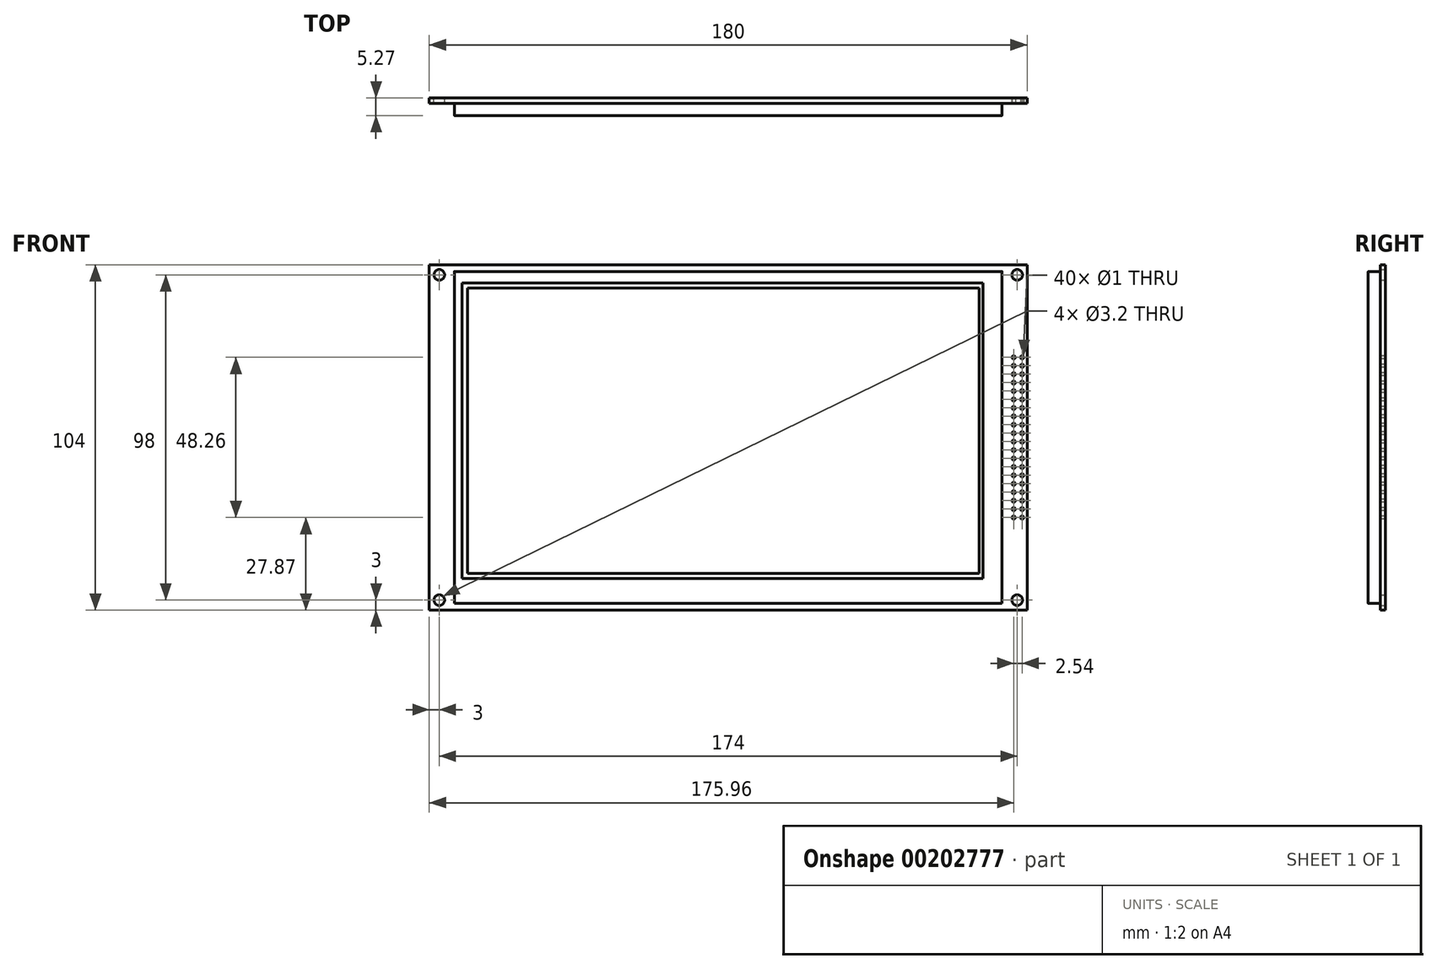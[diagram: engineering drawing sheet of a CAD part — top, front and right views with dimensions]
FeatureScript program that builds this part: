
annotation { "Feature Type Name" : "Feature", "Feature Type Description" : "" }
export const myFeature = defineFeature(function(context is Context, id is Id, definition is map)
    precondition{}
    {
        {
            var Q0;
            Q0=qCreatedBy(makeId("Front.planeOp"),FACE);
            var sketch = newSketch(context, id + "F0", { "sketchPlane" : qUnion([Q0])});
            skLineSegment(sketch, "E0.bottom", {"start": v(90, -52) * mm, "end": v(-90, -52) * mm});
            skLineSegment(sketch, "E0.top", {"start": v(90, 52) * mm, "end": v(-90, 52) * mm});
            skLineSegment(sketch, "E0.left", {"start": v(90, -52) * mm, "end": v(90, 52) * mm});
            skLineSegment(sketch, "E0.right", {"start": v(-90, -52) * mm, "end": v(-90, 52) * mm});
            skPoint(sketch, "E0.middle", {"position": v(0, 0) * mm});
            skCircle(sketch, "E1", {"center": v(-87, -49) * mm, "radius": 1.6 * mm});
            skCircle(sketch, "E2.0.1.0", {"center": v(-87, 49) * mm, "radius": 1.6 * mm});
            skCircle(sketch, "E2.1.0.0", {"center": v(87, -49) * mm, "radius": 1.6 * mm});
            skCircle(sketch, "E2.1.1.0", {"center": v(87, 49) * mm, "radius": 1.6 * mm});
            skLineSegment(sketch, "E2.direction1", {"start": v(-87, -49) * mm, "end": v(87, -49) * mm, "construction": true});
            skLineSegment(sketch, "E2.direction2", {"start": v(-87, -49) * mm, "end": v(-87, 49) * mm, "construction": true});
            skSolve(sketch);
        }
        {
            var Q0;
            Q0=makeQuery(id+"F0.imprint","IMPRINT",FACE,{"disambiguationData":[TD([[makeQuery(id+"F0.imprint","IMPRINT",EDGE,{"derivedFrom":sQuery(id+"F0.wireOp",EDGE,"E0.bottom")}),-1.0]])]});
            extrude(context, id + "F1", {"entities" : qUnion([Q0]), "depth" : 1.57 * mm});
        }
        {
            var Q0;
            Q0=makeQuery(id+"F1.opExtrude","CAP_FACE",FACE,{"disambiguationData":[OSD([sQuery(id+"F0.wireOp",EDGE,"E0.bottom"),sQuery(id+"F0.wireOp",EDGE,"E0.top"),sQuery(id+"F0.wireOp",EDGE,"E0.left"),sQuery(id+"F0.wireOp",EDGE,"E0.right"),sQuery(id+"F0.wireOp",EDGE,"E1"),sQuery(id+"F0.wireOp",EDGE,"E2.0.1.0"),sQuery(id+"F0.wireOp",EDGE,"E2.1.0.0"),sQuery(id+"F0.wireOp",EDGE,"E2.1.1.0")])],"isStart":false});
            var sketch = newSketch(context, id + "F2", { "sketchPlane" : qUnion([Q0])});
            skLineSegment(sketch, "E3", {"start": v(-82.45, -50) * mm, "end": v(82.45, -50) * mm});
            skLineSegment(sketch, "E4", {"start": v(-82.45, -50) * mm, "end": v(-82.45, 50) * mm});
            skLineSegment(sketch, "E5", {"start": v(-82.45, 50) * mm, "end": v(82.45, 50) * mm});
            skLineSegment(sketch, "E6", {"start": v(82.45, 50) * mm, "end": v(82.45, -50) * mm});
            skSolve(sketch);
        }
        {
            var Q0;
            Q0=makeQuery(id+"F2.imprint","IMPRINT",FACE,{"disambiguationData":[TD([[makeQuery(id+"F2.imprint","IMPRINT",EDGE,{"derivedFrom":sQuery(id+"F2.wireOp",EDGE,"E3")}),1.0]])]});
            extrude(context, id + "F3", {"entities" : qUnion([Q0]), "operationType" : NewBodyOperationType.ADD, "depth" : 3.7 * mm});
        }
        {
            var Q0;
            Q0=makeQuery(id+"F3.opExtrude","CAP_FACE",FACE,{"disambiguationData":[OSD([sQuery(id+"F2.wireOp",EDGE,"E3"),sQuery(id+"F2.wireOp",EDGE,"E4"),sQuery(id+"F2.wireOp",EDGE,"E5"),sQuery(id+"F2.wireOp",EDGE,"E6")])],"isStart":false});
            var sketch = newSketch(context, id + "F4", { "sketchPlane" : qUnion([Q0])});
            skLineSegment(sketch, "E7", {"start": v(-80.15, -42.5) * mm, "end": v(76.75, -42.5) * mm});
            skLineSegment(sketch, "E8", {"start": v(-80.15, -42.5) * mm, "end": v(-80.15, 46.5) * mm});
            skLineSegment(sketch, "E9", {"start": v(-80.15, 46.5) * mm, "end": v(76.75, 46.5) * mm});
            skLineSegment(sketch, "E10", {"start": v(76.75, 46.5) * mm, "end": v(76.75, -42.5) * mm});
            skSolve(sketch);
        }
        {
            var Q0;
            Q0=makeQuery(id+"F4.imprint","IMPRINT",FACE,{"disambiguationData":[TD([[makeQuery(id+"F4.imprint","IMPRINT",EDGE,{"derivedFrom":sQuery(id+"F4.wireOp",EDGE,"E7")}),1.0]])]});
            extrude(context, id + "F5", {"entities" : qUnion([Q0]), "operationType" : NewBodyOperationType.REMOVE, "oppositeDirection" : true, "depth" : .2 * mm});
        }
        {
            var Q0;
            Q0=makeQuery(id+"F5.boolean.opBoolean","COPY",FACE,{"derivedFrom":makeQuery(id+"F5.opExtrude","CAP_FACE",FACE,{"disambiguationData":[OSD([sQuery(id+"F4.wireOp",EDGE,"E7"),sQuery(id+"F4.wireOp",EDGE,"E8"),sQuery(id+"F4.wireOp",EDGE,"E9"),sQuery(id+"F4.wireOp",EDGE,"E10")])],"isStart":false})});
            var sketch = newSketch(context, id + "F6", { "sketchPlane" : qUnion([Q0])});
            skLineSegment(sketch, "E11.bottom", {"start": v(-78.53, -40.96) * mm, "end": v(75.55, -40.96) * mm});
            skLineSegment(sketch, "E11.top", {"start": v(-78.53, 44.96) * mm, "end": v(75.55, 44.96) * mm});
            skLineSegment(sketch, "E11.left", {"start": v(-78.53, -40.96) * mm, "end": v(-78.53, 44.96) * mm});
            skLineSegment(sketch, "E11.right", {"start": v(75.55, -40.96) * mm, "end": v(75.55, 44.96) * mm});
            skSolve(sketch);
        }
        {
            var Q0;
            Q0=makeQuery(id+"F6.imprint","IMPRINT",FACE,{"disambiguationData":[TD([[makeQuery(id+"F6.imprint","IMPRINT",EDGE,{"derivedFrom":sQuery(id+"F6.wireOp",EDGE,"E11.bottom")}),1.0]])]});
            extrude(context, id + "F7", {"entities" : qUnion([Q0]), "operationType" : NewBodyOperationType.ADD, "depth" : .1 * mm});
        }
        {
            var Q0;
            Q0=makeQuery(id+"F3.opExtrude","CAP_EDGE",EDGE,{"disambiguationData":[OSD([sQuery(id+"F2.wireOp",EDGE,"E4")])],"isStart":false});
            var Q1;
            Q1=makeQuery(id+"F3.opExtrude","CAP_EDGE",EDGE,{"disambiguationData":[OSD([sQuery(id+"F2.wireOp",EDGE,"E5")])],"isStart":false});
            var Q2;
            Q2=makeQuery(id+"F3.opExtrude","CAP_EDGE",EDGE,{"disambiguationData":[OSD([sQuery(id+"F2.wireOp",EDGE,"E3")])],"isStart":false});
            var Q3;
            Q3=makeQuery(id+"F3.opExtrude","CAP_EDGE",EDGE,{"disambiguationData":[OSD([sQuery(id+"F2.wireOp",EDGE,"E6")])],"isStart":false});
            fillet(context, id + "F8", {"entities" : qUnion([Q0, Q1, Q2, Q3]), "radius" : .1 * mm, "tangentPropagation" : true, "allowEdgeOverflow" : false});
        }
        {
            var Q0;
            Q0=makeQuery(id+"F1.opExtrude","CAP_FACE",FACE,{"disambiguationData":[OSD([sQuery(id+"F0.wireOp",EDGE,"E0.bottom"),sQuery(id+"F0.wireOp",EDGE,"E0.top"),sQuery(id+"F0.wireOp",EDGE,"E0.left"),sQuery(id+"F0.wireOp",EDGE,"E0.right"),sQuery(id+"F0.wireOp",EDGE,"E1"),sQuery(id+"F0.wireOp",EDGE,"E2.0.1.0"),sQuery(id+"F0.wireOp",EDGE,"E2.1.0.0"),sQuery(id+"F0.wireOp",EDGE,"E2.1.1.0")])],"isStart":false});
            var sketch = newSketch(context, id + "F9", { "sketchPlane" : qUnion([Q0])});
            skCircle(sketch, "E12", {"center": v(85.96, -24.13) * mm, "radius": 0.5 * mm});
            skCircle(sketch, "E13.0.1.0", {"center": v(85.96, -21.59) * mm, "radius": 0.5 * mm});
            skCircle(sketch, "E13.0.2.0", {"center": v(85.96, -19.05) * mm, "radius": 0.5 * mm});
            skCircle(sketch, "E13.0.3.0", {"center": v(85.96, -16.5) * mm, "radius": 0.5 * mm});
            skCircle(sketch, "E13.0.4.0", {"center": v(85.96, -13.97) * mm, "radius": 0.5 * mm});
            skCircle(sketch, "E13.0.5.0", {"center": v(85.96, -11.43) * mm, "radius": 0.5 * mm});
            skCircle(sketch, "E13.0.6.0", {"center": v(85.96, -8.89) * mm, "radius": 0.5 * mm});
            skCircle(sketch, "E13.0.7.0", {"center": v(85.96, -6.35) * mm, "radius": 0.5 * mm});
            skCircle(sketch, "E13.0.8.0", {"center": v(85.96, -3.8) * mm, "radius": 0.5 * mm});
            skCircle(sketch, "E13.0.9.0", {"center": v(85.96, -1.27) * mm, "radius": 0.5 * mm});
            skCircle(sketch, "E13.0.10.0", {"center": v(85.96, 1.27) * mm, "radius": 0.5 * mm});
            skCircle(sketch, "E13.0.11.0", {"center": v(85.96, 3.81) * mm, "radius": 0.5 * mm});
            skCircle(sketch, "E13.0.12.0", {"center": v(85.96, 6.35) * mm, "radius": 0.5 * mm});
            skCircle(sketch, "E13.0.13.0", {"center": v(85.96, 8.9) * mm, "radius": 0.5 * mm});
            skCircle(sketch, "E13.0.14.0", {"center": v(85.96, 11.43) * mm, "radius": 0.5 * mm});
            skCircle(sketch, "E13.0.15.0", {"center": v(85.96, 13.97) * mm, "radius": 0.5 * mm});
            skCircle(sketch, "E13.0.16.0", {"center": v(85.96, 16.51) * mm, "radius": 0.5 * mm});
            skCircle(sketch, "E13.0.17.0", {"center": v(85.96, 19.05) * mm, "radius": 0.5 * mm});
            skCircle(sketch, "E13.0.18.0", {"center": v(85.96, 21.6) * mm, "radius": 0.5 * mm});
            skCircle(sketch, "E13.0.19.0", {"center": v(85.96, 24.13) * mm, "radius": 0.5 * mm});
            skCircle(sketch, "E13.1.0.0", {"center": v(88.5, -24.13) * mm, "radius": 0.5 * mm});
            skCircle(sketch, "E13.1.1.0", {"center": v(88.5, -21.59) * mm, "radius": 0.5 * mm});
            skCircle(sketch, "E13.1.2.0", {"center": v(88.5, -19.05) * mm, "radius": 0.5 * mm});
            skCircle(sketch, "E13.1.3.0", {"center": v(88.5, -16.5) * mm, "radius": 0.5 * mm});
            skCircle(sketch, "E13.1.4.0", {"center": v(88.5, -13.97) * mm, "radius": 0.5 * mm});
            skCircle(sketch, "E13.1.5.0", {"center": v(88.5, -11.43) * mm, "radius": 0.5 * mm});
            skCircle(sketch, "E13.1.6.0", {"center": v(88.5, -8.89) * mm, "radius": 0.5 * mm});
            skCircle(sketch, "E13.1.7.0", {"center": v(88.5, -6.35) * mm, "radius": 0.5 * mm});
            skCircle(sketch, "E13.1.8.0", {"center": v(88.5, -3.8) * mm, "radius": 0.5 * mm});
            skCircle(sketch, "E13.1.9.0", {"center": v(88.5, -1.27) * mm, "radius": 0.5 * mm});
            skCircle(sketch, "E13.1.10.0", {"center": v(88.5, 1.27) * mm, "radius": 0.5 * mm});
            skCircle(sketch, "E13.1.11.0", {"center": v(88.5, 3.81) * mm, "radius": 0.5 * mm});
            skCircle(sketch, "E13.1.12.0", {"center": v(88.5, 6.35) * mm, "radius": 0.5 * mm});
            skCircle(sketch, "E13.1.13.0", {"center": v(88.5, 8.9) * mm, "radius": 0.5 * mm});
            skCircle(sketch, "E13.1.14.0", {"center": v(88.5, 11.43) * mm, "radius": 0.5 * mm});
            skCircle(sketch, "E13.1.15.0", {"center": v(88.5, 13.97) * mm, "radius": 0.5 * mm});
            skCircle(sketch, "E13.1.16.0", {"center": v(88.5, 16.51) * mm, "radius": 0.5 * mm});
            skCircle(sketch, "E13.1.17.0", {"center": v(88.5, 19.05) * mm, "radius": 0.5 * mm});
            skCircle(sketch, "E13.1.18.0", {"center": v(88.5, 21.6) * mm, "radius": 0.5 * mm});
            skCircle(sketch, "E13.1.19.0", {"center": v(88.5, 24.13) * mm, "radius": 0.5 * mm});
            skLineSegment(sketch, "E13.direction1", {"start": v(85.96, -24.13) * mm, "end": v(88.5, -24.13) * mm, "construction": true});
            skLineSegment(sketch, "E13.direction2", {"start": v(85.96, -24.13) * mm, "end": v(85.96, -21.59) * mm, "construction": true});
            skSolve(sketch);
        }
        {
            var Q0;
            Q0=makeQuery(id+"F9.imprint","IMPRINT",FACE,{"disambiguationData":[TD([[makeQuery(id+"F9.imprint","IMPRINT",EDGE,{"derivedFrom":sQuery(id+"F9.wireOp",EDGE,"E13.0.15.0")}),1.0]])]});
            var Q1;
            Q1=makeQuery(id+"F9.imprint","IMPRINT",FACE,{"disambiguationData":[TD([[makeQuery(id+"F9.imprint","IMPRINT",EDGE,{"derivedFrom":sQuery(id+"F9.wireOp",EDGE,"E13.0.13.0")}),1.0]])]});
            var Q2;
            Q2=makeQuery(id+"F9.imprint","IMPRINT",FACE,{"disambiguationData":[TD([[makeQuery(id+"F9.imprint","IMPRINT",EDGE,{"derivedFrom":sQuery(id+"F9.wireOp",EDGE,"E13.0.14.0")}),1.0]])]});
            var Q3;
            Q3=makeQuery(id+"F9.imprint","IMPRINT",FACE,{"disambiguationData":[TD([[makeQuery(id+"F9.imprint","IMPRINT",EDGE,{"derivedFrom":sQuery(id+"F9.wireOp",EDGE,"E13.0.2.0")}),1.0]])]});
            var Q4;
            Q4=makeQuery(id+"F9.imprint","IMPRINT",FACE,{"disambiguationData":[TD([[makeQuery(id+"F9.imprint","IMPRINT",EDGE,{"derivedFrom":sQuery(id+"F9.wireOp",EDGE,"E13.0.3.0")}),1.0]])]});
            var Q5;
            Q5=makeQuery(id+"F9.imprint","IMPRINT",FACE,{"disambiguationData":[TD([[makeQuery(id+"F9.imprint","IMPRINT",EDGE,{"derivedFrom":sQuery(id+"F9.wireOp",EDGE,"E13.0.4.0")}),1.0]])]});
            var Q6;
            Q6=makeQuery(id+"F9.imprint","IMPRINT",FACE,{"disambiguationData":[TD([[makeQuery(id+"F9.imprint","IMPRINT",EDGE,{"derivedFrom":sQuery(id+"F9.wireOp",EDGE,"E13.0.5.0")}),1.0]])]});
            var Q7;
            Q7=makeQuery(id+"F9.imprint","IMPRINT",FACE,{"disambiguationData":[TD([[makeQuery(id+"F9.imprint","IMPRINT",EDGE,{"derivedFrom":sQuery(id+"F9.wireOp",EDGE,"E13.0.6.0")}),1.0]])]});
            var Q8;
            Q8=makeQuery(id+"F9.imprint","IMPRINT",FACE,{"disambiguationData":[TD([[makeQuery(id+"F9.imprint","IMPRINT",EDGE,{"derivedFrom":sQuery(id+"F9.wireOp",EDGE,"E13.0.7.0")}),1.0]])]});
            var Q9;
            Q9=makeQuery(id+"F9.imprint","IMPRINT",FACE,{"disambiguationData":[TD([[makeQuery(id+"F9.imprint","IMPRINT",EDGE,{"derivedFrom":sQuery(id+"F9.wireOp",EDGE,"E13.0.8.0")}),1.0]])]});
            var Q10;
            Q10=makeQuery(id+"F9.imprint","IMPRINT",FACE,{"disambiguationData":[TD([[makeQuery(id+"F9.imprint","IMPRINT",EDGE,{"derivedFrom":sQuery(id+"F9.wireOp",EDGE,"E13.0.9.0")}),1.0]])]});
            var Q11;
            Q11=makeQuery(id+"F9.imprint","IMPRINT",FACE,{"disambiguationData":[TD([[makeQuery(id+"F9.imprint","IMPRINT",EDGE,{"derivedFrom":sQuery(id+"F9.wireOp",EDGE,"E13.0.11.0")}),1.0]])]});
            var Q12;
            Q12=makeQuery(id+"F9.imprint","IMPRINT",FACE,{"disambiguationData":[TD([[makeQuery(id+"F9.imprint","IMPRINT",EDGE,{"derivedFrom":sQuery(id+"F9.wireOp",EDGE,"E13.1.3.0")}),1.0]])]});
            var Q13;
            Q13=makeQuery(id+"F9.imprint","IMPRINT",FACE,{"disambiguationData":[TD([[makeQuery(id+"F9.imprint","IMPRINT",EDGE,{"derivedFrom":sQuery(id+"F9.wireOp",EDGE,"E13.0.12.0")}),1.0]])]});
            var Q14;
            Q14=makeQuery(id+"F9.imprint","IMPRINT",FACE,{"disambiguationData":[TD([[makeQuery(id+"F9.imprint","IMPRINT",EDGE,{"derivedFrom":sQuery(id+"F9.wireOp",EDGE,"E13.0.16.0")}),1.0]])]});
            var Q15;
            Q15=makeQuery(id+"F9.imprint","IMPRINT",FACE,{"disambiguationData":[TD([[makeQuery(id+"F9.imprint","IMPRINT",EDGE,{"derivedFrom":sQuery(id+"F9.wireOp",EDGE,"E13.1.17.0")}),1.0]])]});
            var Q16;
            Q16=makeQuery(id+"F9.imprint","IMPRINT",FACE,{"disambiguationData":[TD([[makeQuery(id+"F9.imprint","IMPRINT",EDGE,{"derivedFrom":sQuery(id+"F9.wireOp",EDGE,"E13.0.17.0")}),1.0]])]});
            var Q17;
            Q17=makeQuery(id+"F9.imprint","IMPRINT",FACE,{"disambiguationData":[TD([[makeQuery(id+"F9.imprint","IMPRINT",EDGE,{"derivedFrom":sQuery(id+"F9.wireOp",EDGE,"E13.0.18.0")}),1.0]])]});
            var Q18;
            Q18=makeQuery(id+"F9.imprint","IMPRINT",FACE,{"disambiguationData":[TD([[makeQuery(id+"F9.imprint","IMPRINT",EDGE,{"derivedFrom":sQuery(id+"F9.wireOp",EDGE,"E13.1.18.0")}),1.0]])]});
            var Q19;
            Q19=makeQuery(id+"F9.imprint","IMPRINT",FACE,{"disambiguationData":[TD([[makeQuery(id+"F9.imprint","IMPRINT",EDGE,{"derivedFrom":sQuery(id+"F9.wireOp",EDGE,"E13.1.2.0")}),1.0]])]});
            var Q20;
            Q20=makeQuery(id+"F9.imprint","IMPRINT",FACE,{"disambiguationData":[TD([[makeQuery(id+"F9.imprint","IMPRINT",EDGE,{"derivedFrom":sQuery(id+"F9.wireOp",EDGE,"E13.0.19.0")}),1.0]])]});
            var Q21;
            Q21=makeQuery(id+"F9.imprint","IMPRINT",FACE,{"disambiguationData":[TD([[makeQuery(id+"F9.imprint","IMPRINT",EDGE,{"derivedFrom":sQuery(id+"F9.wireOp",EDGE,"E13.1.15.0")}),1.0]])]});
            var Q22;
            Q22=makeQuery(id+"F9.imprint","IMPRINT",FACE,{"disambiguationData":[TD([[makeQuery(id+"F9.imprint","IMPRINT",EDGE,{"derivedFrom":sQuery(id+"F9.wireOp",EDGE,"E13.1.6.0")}),1.0]])]});
            var Q23;
            Q23=makeQuery(id+"F9.imprint","IMPRINT",FACE,{"disambiguationData":[TD([[makeQuery(id+"F9.imprint","IMPRINT",EDGE,{"derivedFrom":sQuery(id+"F9.wireOp",EDGE,"E13.1.9.0")}),1.0]])]});
            var Q24;
            Q24=makeQuery(id+"F9.imprint","IMPRINT",FACE,{"disambiguationData":[TD([[makeQuery(id+"F9.imprint","IMPRINT",EDGE,{"derivedFrom":sQuery(id+"F9.wireOp",EDGE,"E13.1.16.0")}),1.0]])]});
            var Q25;
            Q25=makeQuery(id+"F9.imprint","IMPRINT",FACE,{"disambiguationData":[TD([[makeQuery(id+"F9.imprint","IMPRINT",EDGE,{"derivedFrom":sQuery(id+"F9.wireOp",EDGE,"E13.0.10.0")}),1.0]])]});
            var Q26;
            Q26=makeQuery(id+"F9.imprint","IMPRINT",FACE,{"disambiguationData":[TD([[makeQuery(id+"F9.imprint","IMPRINT",EDGE,{"derivedFrom":sQuery(id+"F9.wireOp",EDGE,"E13.1.19.0")}),1.0]])]});
            var Q27;
            Q27=makeQuery(id+"F9.imprint","IMPRINT",FACE,{"disambiguationData":[TD([[makeQuery(id+"F9.imprint","IMPRINT",EDGE,{"derivedFrom":sQuery(id+"F9.wireOp",EDGE,"E13.1.12.0")}),1.0]])]});
            var Q28;
            Q28=makeQuery(id+"F9.imprint","IMPRINT",FACE,{"disambiguationData":[TD([[makeQuery(id+"F9.imprint","IMPRINT",EDGE,{"derivedFrom":sQuery(id+"F9.wireOp",EDGE,"E13.1.7.0")}),1.0]])]});
            var Q29;
            Q29=makeQuery(id+"F9.imprint","IMPRINT",FACE,{"disambiguationData":[TD([[makeQuery(id+"F9.imprint","IMPRINT",EDGE,{"derivedFrom":sQuery(id+"F9.wireOp",EDGE,"E13.1.1.0")}),1.0]])]});
            var Q30;
            Q30=makeQuery(id+"F9.imprint","IMPRINT",FACE,{"disambiguationData":[TD([[makeQuery(id+"F9.imprint","IMPRINT",EDGE,{"derivedFrom":sQuery(id+"F9.wireOp",EDGE,"E13.1.10.0")}),1.0]])]});
            var Q31;
            Q31=makeQuery(id+"F9.imprint","IMPRINT",FACE,{"disambiguationData":[TD([[makeQuery(id+"F9.imprint","IMPRINT",EDGE,{"derivedFrom":sQuery(id+"F9.wireOp",EDGE,"E13.1.4.0")}),1.0]])]});
            var Q32;
            Q32=makeQuery(id+"F9.imprint","IMPRINT",FACE,{"disambiguationData":[TD([[makeQuery(id+"F9.imprint","IMPRINT",EDGE,{"derivedFrom":sQuery(id+"F9.wireOp",EDGE,"E13.1.13.0")}),1.0]])]});
            var Q33;
            Q33=makeQuery(id+"F9.imprint","IMPRINT",FACE,{"disambiguationData":[TD([[makeQuery(id+"F9.imprint","IMPRINT",EDGE,{"derivedFrom":sQuery(id+"F9.wireOp",EDGE,"E13.1.8.0")}),1.0]])]});
            var Q34;
            Q34=makeQuery(id+"F9.imprint","IMPRINT",FACE,{"disambiguationData":[TD([[makeQuery(id+"F9.imprint","IMPRINT",EDGE,{"derivedFrom":sQuery(id+"F9.wireOp",EDGE,"E13.1.11.0")}),1.0]])]});
            var Q35;
            Q35=makeQuery(id+"F9.imprint","IMPRINT",FACE,{"disambiguationData":[TD([[makeQuery(id+"F9.imprint","IMPRINT",EDGE,{"derivedFrom":sQuery(id+"F9.wireOp",EDGE,"E13.1.5.0")}),1.0]])]});
            var Q36;
            Q36=makeQuery(id+"F9.imprint","IMPRINT",FACE,{"disambiguationData":[TD([[makeQuery(id+"F9.imprint","IMPRINT",EDGE,{"derivedFrom":sQuery(id+"F9.wireOp",EDGE,"E13.1.14.0")}),1.0]])]});
            var Q37;
            Q37=makeQuery(id+"F9.imprint","IMPRINT",FACE,{"disambiguationData":[TD([[makeQuery(id+"F9.imprint","IMPRINT",EDGE,{"derivedFrom":sQuery(id+"F9.wireOp",EDGE,"E12")}),1.0]])]});
            var Q38;
            Q38=makeQuery(id+"F9.imprint","IMPRINT",FACE,{"disambiguationData":[TD([[makeQuery(id+"F9.imprint","IMPRINT",EDGE,{"derivedFrom":sQuery(id+"F9.wireOp",EDGE,"E13.1.0.0")}),1.0]])]});
            var Q39;
            Q39=makeQuery(id+"F9.imprint","IMPRINT",FACE,{"disambiguationData":[TD([[makeQuery(id+"F9.imprint","IMPRINT",EDGE,{"derivedFrom":sQuery(id+"F9.wireOp",EDGE,"E13.0.1.0")}),1.0]])]});
            extrude(context, id + "F10", {"entities" : qUnion([Q0, Q1, Q2, Q3, Q4, Q5, Q6, Q7, Q8, Q9, Q10, Q11, Q12, Q13, Q14, Q15, Q16, Q17, Q18, Q19, Q20, Q21, Q22, Q23, Q24, Q25, Q26, Q27, Q28, Q29, Q30, Q31, Q32, Q33, Q34, Q35, Q36, Q37, Q38, Q39]), "operationType" : NewBodyOperationType.REMOVE, "endBound" : BoundingType.THROUGH_ALL, "oppositeDirection" : true, "depth" : 25 * mm});
        }
    });
